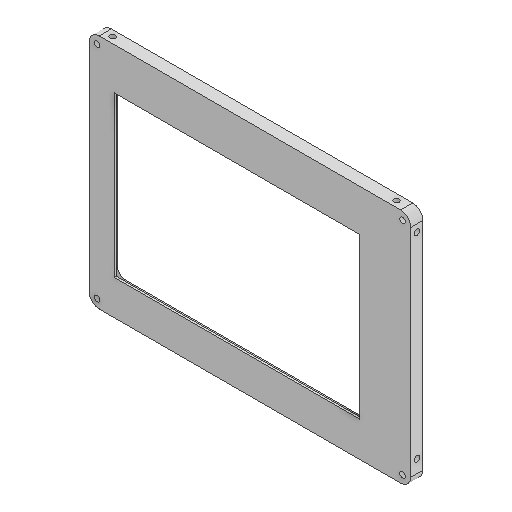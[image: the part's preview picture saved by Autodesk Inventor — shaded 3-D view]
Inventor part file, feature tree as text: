
AUTODESK INVENTOR PART (.ipt)
format: ipt  version: 2022 (Build 260153000, 153)  size: 251,392 bytes
history: native  units: mm
features: sketch x7, extrude x6, reference x6, other x4, projected_geometry x2, hole x1
ambient origin geometry x8: Origin, YZ Plane, XZ Plane, XY Plane, X Axis, Y Axis, Z Axis, Center Point
bodies: Volumenkörper1 (feature_tree)
feature tree (26):
  extrude  "Extrusion1"  Depth=2.0mm
  extrude  "Extrusion2"  Depth=5.0mm
  hole  "Bohrung1"  [1 undecoded]
  extrude  "Extrusion3"  Depth=2.8mm
  extrude  "Extrusion4"  Depth=2.8mm
  extrude  "Extrusion5"  Depth=4.0mm
  extrude  "Extrusion6"  Depth=20.0mm
  sketch  "Skizze1"  dims[d0=1.0mm d1=2.0mm]
  reference  "Referenz1"
  reference  "Referenz2"
  sketch  "Skizze2"  dims[d2=5.0mm d3=5.0mm]
  reference  "Referenz3"
  projected_geometry  "Projizierte Kontur1"
  sketch  "Skizze3"  dims[d5=0.0mm d6=1.0mm]
  projected_geometry  "Projizierte Kontur2"
  sketch  "Skizze4"  dims[d8=0.0mm d9=2.8mm]
  reference  "Referenz4"
  sketch  "Skizze5"  dims[d10=2.8mm d11=2.8mm]
  sketch  "Skizze6"  dims[d12=2.8mm d13=4.0mm]
  reference  "Referenz5"
  reference  "Referenz6"
  sketch  "Skizze7"  dims[d14=4.0mm d15=4.0mm d16=4.0mm d17=4.0mm d18=4.0mm d19=4.0mm d20=4.0mm d21=2.8mm d22=6.0mm d23=7.0mm d24=9.0mm d25=90.0deg d26=8.0mm d27=20.594885mm d28=2.8mm d29=3.0mm d30=2.8mm d31=20.0mm d32=0.0mm d33=20.0mm d34=0.0mm d35=2.8mm d36=3.0mm d37=2.8mm d38=20.0mm d39=0.0mm d40=20.0mm d41=0.0mm]
  other  "Omnicscope_Xiao.iam"
  other  "00_24wellplate_base:1"
  other  "Omniscope_USBC_Base_Top+:1"
  other  "Omniscope_USBC_Base:1"
note: 1 required parameter value undecoded (feature->parameter linkage not recoverable at this tier; creation-order binding heuristic only, values carry confidence <= 0.55)
